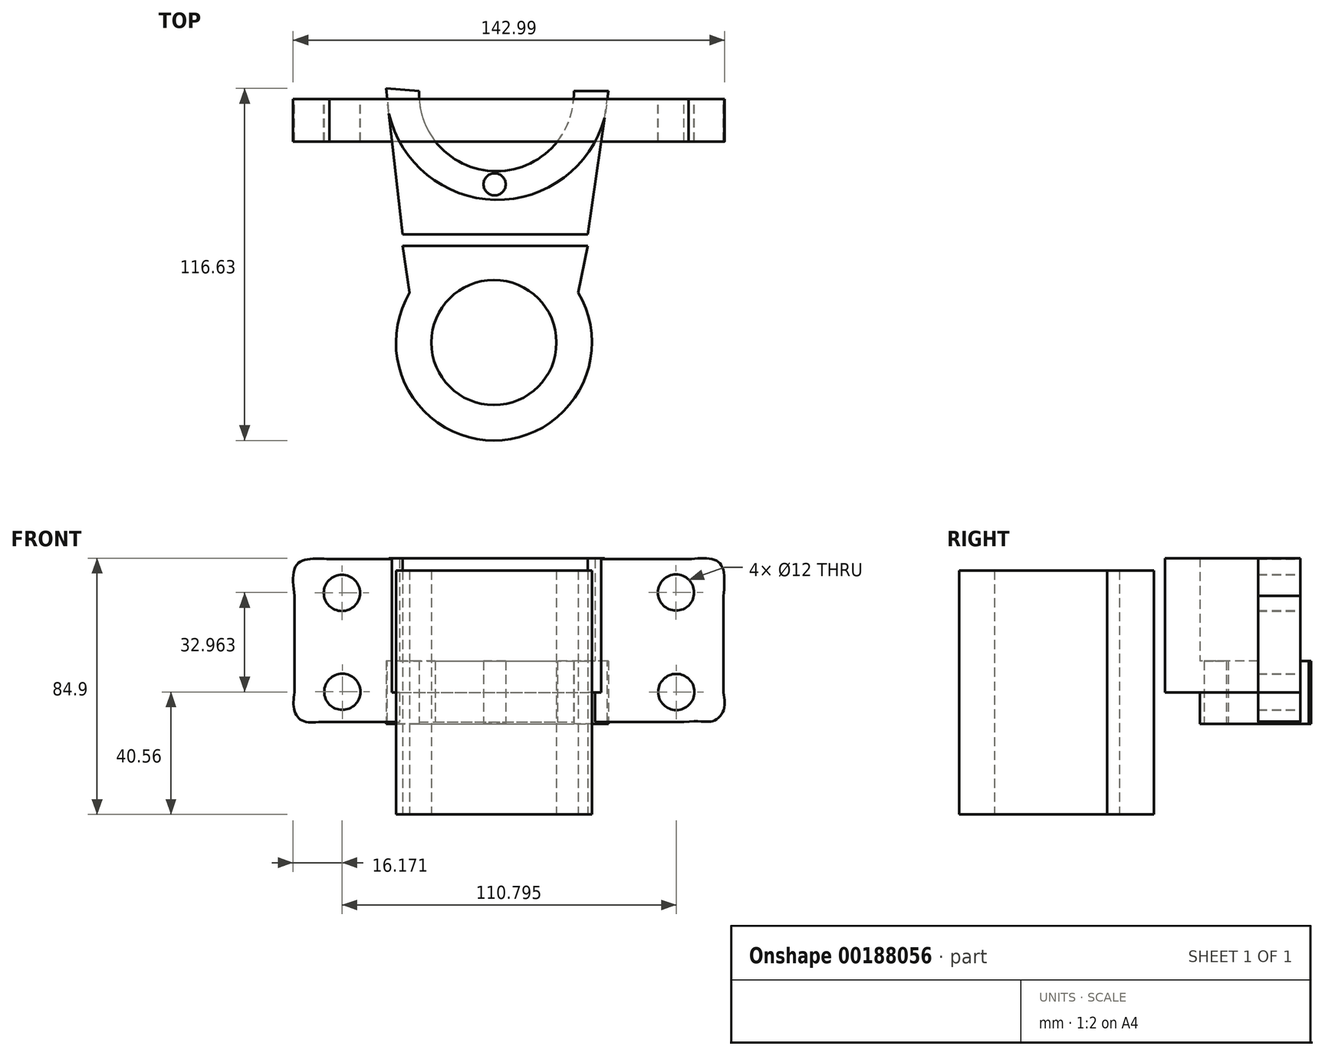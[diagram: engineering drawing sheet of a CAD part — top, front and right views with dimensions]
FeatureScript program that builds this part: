
annotation { "Feature Type Name" : "Feature", "Feature Type Description" : "" }
export const myFeature = defineFeature(function(context is Context, id is Id, definition is map)
    precondition{}
    {
        {
            var Q0;
            Q0=qCreatedBy(makeId("Front.planeOp"),FACE);
            var sketch = newSketch(context, id + "F0", { "sketchPlane" : qUnion([Q0])});
            skLineSegment(sketch, "E0", {"start": v(61.01, 44.16) * mm, "end": v(-57.99, 44.16) * mm});
            skFitSpline(sketch, "E1", {"points": [v(61.01, 44.16) * mm, v(68.83, 44.16) * mm, v(72.3, 41.32) * mm, v(72.6, 32) * mm], "startDerivative": vector(23.49, 2.36) * mm, "endDerivative": vector(-2.08, -24.38) * mm});
            skFitSpline(sketch, "E2", {"points": [v(-57.99, 44.16) * mm, v(-64.85, 44.16) * mm, v(-69.27, 41.64) * mm, v(-69.58, 32) * mm], "startDerivative": vector(-20.84, 1.61) * mm, "endDerivative": vector(3.01, -25.54) * mm});
            skLineSegment(sketch, "E3", {"start": v(72.6, 32) * mm, "end": v(72.6, 0) * mm});
            skLineSegment(sketch, "E4", {"start": v(-69.58, 32) * mm, "end": v(-69.58, 0) * mm});
            skFitSpline(sketch, "E5", {"points": [v(72.6, 0) * mm, v(72.6, -5.97) * mm, v(69.14, -9.44) * mm, v(59.5, -9.76) * mm], "startDerivative": vector(2.68, -18.77) * mm, "endDerivative": vector(-43.88, -4.73) * mm});
            skFitSpline(sketch, "E6", {"points": [v(-69.58, 0) * mm, v(-69.58, -5.97) * mm, v(-66.74, -9.44) * mm, v(-59.5, -9.76) * mm], "startDerivative": vector(-2.14, -18.7) * mm, "endDerivative": vector(25.47, 0) * mm});
            skCircle(sketch, "E7", {"center": v(56.85, 33.12) * mm, "radius": 6 * mm});
            skCircle(sketch, "E8", {"center": v(56.96, 0.16) * mm, "radius": 6 * mm});
            skCircle(sketch, "E9", {"center": v(-53.84, 32.98) * mm, "radius": 6 * mm});
            skCircle(sketch, "E10", {"center": v(-53.7, 0.23) * mm, "radius": 6 * mm});
            skLineSegment(sketch, "E11", {"start": v(59.5, -9.76) * mm, "end": v(36.83, -9.76) * mm});
            skLineSegment(sketch, "E12", {"start": v(-59.5, -9.76) * mm, "end": v(-39.32, -9.76) * mm});
            skLineSegment(sketch, "E13", {"start": v(-39.32, -9.76) * mm, "end": v(36.83, -9.76) * mm});
            skSolve(sketch);
        }
        {
            var Q0;
            Q0=qCreatedBy(makeId("Top.planeOp"),FACE);
            var sketch = newSketch(context, id + "F1", { "sketchPlane" : qUnion([Q0])});
            skArc(sketch, "E14", {"start": v(-39.23, 3.57) * mm, "mid": v(-2.77, -33.33) * mm, "end": v(34.5, 2.74) * mm});
            skArc(sketch, "E15", {"start": v(-28.3, 2.74) * mm, "mid": v(-2.65, -23.86) * mm, "end": v(22.99, 2.74) * mm});
            skCircle(sketch, "E16", {"center": v(-3.24, -28.21) * mm, "radius": 3.67 * mm});
            skLineSegment(sketch, "E17", {"start": v(-39.23, 3.57) * mm, "end": v(-33.76, -44.79) * mm});
            skLineSegment(sketch, "E18", {"start": v(34.5, 2.74) * mm, "end": v(27.6, -44.79) * mm});
            skLineSegment(sketch, "E19", {"start": v(-33.76, -44.79) * mm, "end": v(27.6, -44.79) * mm});
            skLineSegment(sketch, "E20", {"start": v(-33.76, -44.79) * mm, "end": v(-33.76, -48.56) * mm});
            skLineSegment(sketch, "E21", {"start": v(-33.76, -48.56) * mm, "end": v(27.6, -48.56) * mm});
            skLineSegment(sketch, "E22", {"start": v(27.6, -48.56) * mm, "end": v(27.6, -44.79) * mm});
            skLineSegment(sketch, "E23", {"start": v(-33.76, -48.56) * mm, "end": v(-31.38, -64.05) * mm});
            skLineSegment(sketch, "E24", {"start": v(27.6, -48.56) * mm, "end": v(24.43, -64.05) * mm});
            skLineSegment(sketch, "E25", {"start": v(34.5, 2.74) * mm, "end": v(22.99, 2.74) * mm});
            skLineSegment(sketch, "E26", {"start": v(-28.3, 2.74) * mm, "end": v(-39.23, 3.57) * mm});
            skCircle(sketch, "E27", {"center": v(-3.48, -80.61) * mm, "radius": 32.45 * mm});
            skPoint(sketch, "E27.third.point", {"position": v(1.59, -48.56) * mm});
            skCircle(sketch, "E28", {"center": v(-3.48, -80.61) * mm, "radius": 20.72 * mm});
            skSolve(sketch);
        }
        {
            var Q0;
            Q0=makeQuery(id+"F0.imprint","IMPRINT",FACE,{"disambiguationData":[TD([[makeQuery(id+"F0.imprint","IMPRINT",EDGE,{"derivedFrom":sQuery(id+"F0.wireOp",EDGE,"E0")}),1.0]])]});
            extrude(context, id + "F2", {"entities" : qUnion([Q0]), "depth" : 14 * mm});
        }
        {
            var Q0;
            Q0=makeQuery(id+"F1.imprint","IMPRINT",FACE,{"disambiguationData":[TD([[makeQuery(id+"F1.imprint","IMPRINT",EDGE,{"derivedFrom":sQuery(id+"F1.wireOp",EDGE,"E15")}),-1.0]])]});
            extrude(context, id + "F3", {"entities" : qUnion([Q0]), "operationType" : NewBodyOperationType.ADD, "endBound" : BoundingType.SYMMETRIC, "depth" : 20.8 * mm});
        }
        {
            var Q0;
            {var subQ5=sQuery(id+"F1.wireOp",EDGE,"E19");Q0=makeQuery(id+"F1.imprint","IMPRINT",FACE,{"disambiguationData":[TD([[makeQuery(id+"F1.imprint","IMPRINT",EDGE,{"derivedFrom":subQ5}),1.0]])]});}
            extrude(context, id + "F4", {"entities" : qUnion([Q0]), "operationType" : NewBodyOperationType.ADD, "depth" : 44.5 * mm});
        }
        {
            var Q0;
            {var subQ0=sQuery(id+"F1.wireOp",EDGE,"E23");Q0=makeQuery(id+"F1.imprint","IMPRINT",FACE,{"disambiguationData":[TD([[makeQuery(id+"F1.imprint","IMPRINT",EDGE,{"derivedFrom":subQ0}),1.0]])]});}
            var Q1;
            {var subQ0=sQuery(id+"F1.wireOp",EDGE,"E24");Q1=makeQuery(id+"F1.imprint","IMPRINT",FACE,{"disambiguationData":[TD([[makeQuery(id+"F1.imprint","IMPRINT",EDGE,{"derivedFrom":subQ0}),-1.0]])]});}
            var Q2;
            Q2=makeQuery(id+"F1.imprint","IMPRINT",FACE,{"disambiguationData":[TD([[makeQuery(id+"F1.imprint","IMPRINT",EDGE,{"derivedFrom":sQuery(id+"F1.wireOp",EDGE,"E28")}),-1.0]])]});
            extrude(context, id + "F5", {"entities" : qUnion([Q0, Q1, Q2]), "endBound" : BoundingType.SYMMETRIC, "depth" : 80.8 * mm});
        }
    });
